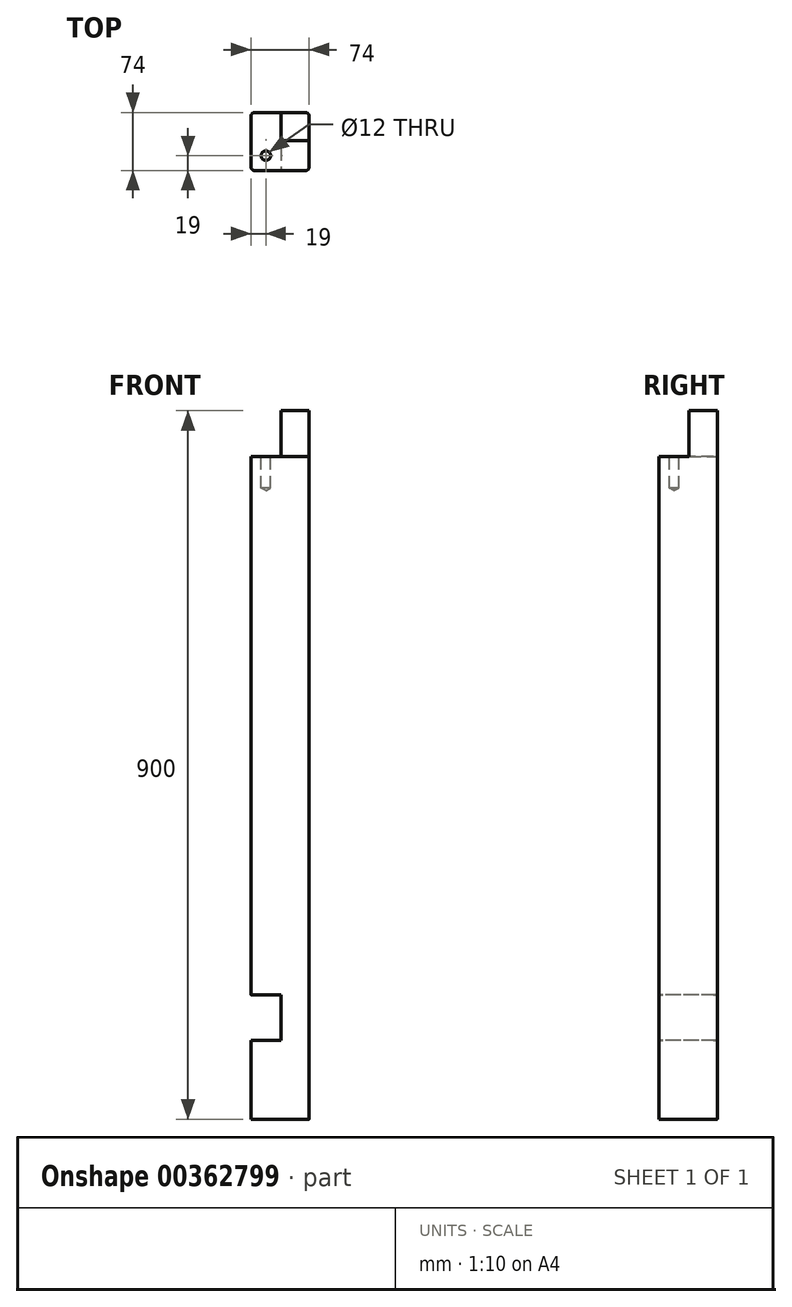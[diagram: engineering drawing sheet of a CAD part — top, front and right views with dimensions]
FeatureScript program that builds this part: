
annotation { "Feature Type Name" : "Feature", "Feature Type Description" : "" }
export const myFeature = defineFeature(function(context is Context, id is Id, definition is map)
    precondition{}
    {
        {
            var Q0;
            Q0=qCreatedBy(makeId("Top.planeOp"),FACE);
            var sketch = newSketch(context, id + "F0", { "sketchPlane" : qUnion([Q0])});
            skLineSegment(sketch, "E0.bottom", {"start": v(37, 37) * mm, "end": v(-37, 37) * mm});
            skLineSegment(sketch, "E0.top", {"start": v(37, -37) * mm, "end": v(-37, -37) * mm});
            skLineSegment(sketch, "E0.left", {"start": v(37, 37) * mm, "end": v(37, -37) * mm});
            skLineSegment(sketch, "E0.right", {"start": v(-37, 37) * mm, "end": v(-37, -37) * mm});
            skPoint(sketch, "E0.middle", {"position": v(0, 0) * mm});
            skSolve(sketch);
        }
        {
            var Q0;
            Q0=makeQuery(id+"F0.imprint","IMPRINT",FACE,{"disambiguationData":[TD([[makeQuery(id+"F0.imprint","IMPRINT",EDGE,{"derivedFrom":sQuery(id+"F0.wireOp",EDGE,"E0.bottom")}),1.0]])]});
            extrude(context, id + "F1", {"entities" : qUnion([Q0]), "oppositeDirection" : true, "depth" : 900 * mm});
        }
        {
            var Q0;
            Q0=makeQuery(id+"F1.opExtrude","SWEPT_FACE",FACE,{"disambiguationData":[OSD([sQuery(id+"F0.wireOp",EDGE,"E0.top")])]});
            var sketch = newSketch(context, id + "F2", { "sketchPlane" : qUnion([Q0])});
            skLineSegment(sketch, "E1", {"start": v(-37, -58) * mm, "end": v(37, -58) * mm});
            skSolve(sketch);
        }
        {
            var Q0;
            Q0=makeQuery(id+"F1.opExtrude","SWEPT_FACE",FACE,{"disambiguationData":[OSD([sQuery(id+"F0.wireOp",EDGE,"E0.right")])]});
            var sketch = newSketch(context, id + "F3", { "sketchPlane" : qUnion([Q0])});
            skLineSegment(sketch, "E2", {"start": v(37, -58) * mm, "end": v(-37, -58) * mm});
            skSolve(sketch);
        }
        {
            var Q0;
            {var subQ0=sQuery(id+"F2.wireOp",EDGE,"E1");Q0=makeQuery(id+"F2.imprint","IMPRINT",FACE,{"disambiguationData":[TD([[makeQuery(id+"F2.imprint","IMPRINT",EDGE,{"derivedFrom":subQ0}),1.0]])]});}
            extrude(context, id + "F4", {"entities" : qUnion([Q0]), "operationType" : NewBodyOperationType.REMOVE, "oppositeDirection" : true, "depth" : 38 * mm});
        }
        {
            var Q0;
            {var subQ0=sQuery(id+"F3.wireOp",EDGE,"E2");Q0=makeQuery(id+"F3.imprint","IMPRINT",FACE,{"disambiguationData":[TD([[makeQuery(id+"F3.imprint","IMPRINT",EDGE,{"derivedFrom":subQ0}),-1.0]])]});}
            extrude(context, id + "F5", {"entities" : qUnion([Q0]), "operationType" : NewBodyOperationType.REMOVE, "oppositeDirection" : true, "depth" : 38 * mm});
        }
        {
            var Q0;
            Q0=makeQuery(id+"F5.boolean.opBoolean","MERGE",FACE,{"derivedFrom":[makeQuery(id+"F4.boolean.opBoolean","COPY",FACE,{"derivedFrom":makeQuery(id+"F4.opExtrude","SWEPT_FACE",FACE,{"disambiguationData":[OSD([sQuery(id+"F2.wireOp",EDGE,"E1")])]})}),makeQuery(id+"F5.opExtrude","SWEPT_FACE",FACE,{"disambiguationData":[OSD([sQuery(id+"F3.wireOp",EDGE,"E2")])]})]});
            var sketch = newSketch(context, id + "F6", { "sketchPlane" : qUnion([Q0])});
            skPoint(sketch, "E3", {"position": v(-18, -18) * mm});
            skSolve(sketch);
        }
        {
            var Q0;
            Q0=sQuery(id+"F6.wireOp",VERTEX,"E3");
            var Q1;
            Q1=makeQuery(id+"F1.opExtrude","SWEPT_BODY",BODY,{"disambiguationData":[OSD([sQuery(id+"F0.wireOp",EDGE,"E0.bottom"),sQuery(id+"F0.wireOp",EDGE,"E0.top"),sQuery(id+"F0.wireOp",EDGE,"E0.left"),sQuery(id+"F0.wireOp",EDGE,"E0.right")])]});
            hole(context, id + "F7", {"style" : HoleStyle.SIMPLE, "endStyle" : HoleEndStyle.BLIND, "holeDiameter" : 12 * mm, "holeDepth" : 40 * mm, "isTappedThrough" : true, "tappedDepth" : 12 * mm, "tapClearance" : 3, "locations" : qUnion([Q0]), "scope" : qUnion([Q1])});
        }
        {
            var Q0;
            Q0=makeQuery(id+"F1.opExtrude","SWEPT_FACE",FACE,{"disambiguationData":[OSD([sQuery(id+"F0.wireOp",EDGE,"E0.right")])]});
            var sketch = newSketch(context, id + "F8", { "sketchPlane" : qUnion([Q0])});
            skLineSegment(sketch, "E4", {"start": v(-37, -742) * mm, "end": v(37, -742) * mm});
            skLineSegment(sketch, "E5", {"start": v(-37, -800) * mm, "end": v(37, -800) * mm});
            skSolve(sketch);
        }
        {
            var Q0;
            {var subQ0=sQuery(id+"F8.wireOp",EDGE,"E4");Q0=makeQuery(id+"F8.imprint","IMPRINT",FACE,{"disambiguationData":[TD([[makeQuery(id+"F8.imprint","IMPRINT",EDGE,{"derivedFrom":subQ0}),-1.0]])]});}
            extrude(context, id + "F9", {"entities" : qUnion([Q0]), "operationType" : NewBodyOperationType.REMOVE, "oppositeDirection" : true, "depth" : 38 * mm});
        }
        {
            var Q0;
            Q0=makeQuery(id+"F1.opExtrude","SWEPT_EDGE",EDGE,{"disambiguationData":[OSD([sQuery(id+"F0.wireOp",EDGE,"E0.top"),sQuery(id+"F0.wireOp",EDGE,"E0.right")])]});
            var Q1;
            Q1=makeQuery(id+"F1.opExtrude","SWEPT_EDGE",EDGE,{"disambiguationData":[OSD([sQuery(id+"F0.wireOp",EDGE,"E0.bottom"),sQuery(id+"F0.wireOp",EDGE,"E0.right")])]});
            var Q2;
            Q2=makeQuery(id+"F1.opExtrude","SWEPT_EDGE",EDGE,{"disambiguationData":[OSD([sQuery(id+"F0.wireOp",EDGE,"E0.top"),sQuery(id+"F0.wireOp",EDGE,"E0.left")])]});
            var Q3;
            Q3=makeQuery(id+"F1.opExtrude","SWEPT_EDGE",EDGE,{"disambiguationData":[OSD([sQuery(id+"F0.wireOp",EDGE,"E0.bottom"),sQuery(id+"F0.wireOp",EDGE,"E0.left")])]});
            fillet(context, id + "F10", {"entities" : qUnion([Q0, Q1, Q2, Q3]), "radius" : 5 * mm, "tangentPropagation" : true, "allowEdgeOverflow" : false});
        }
    });
